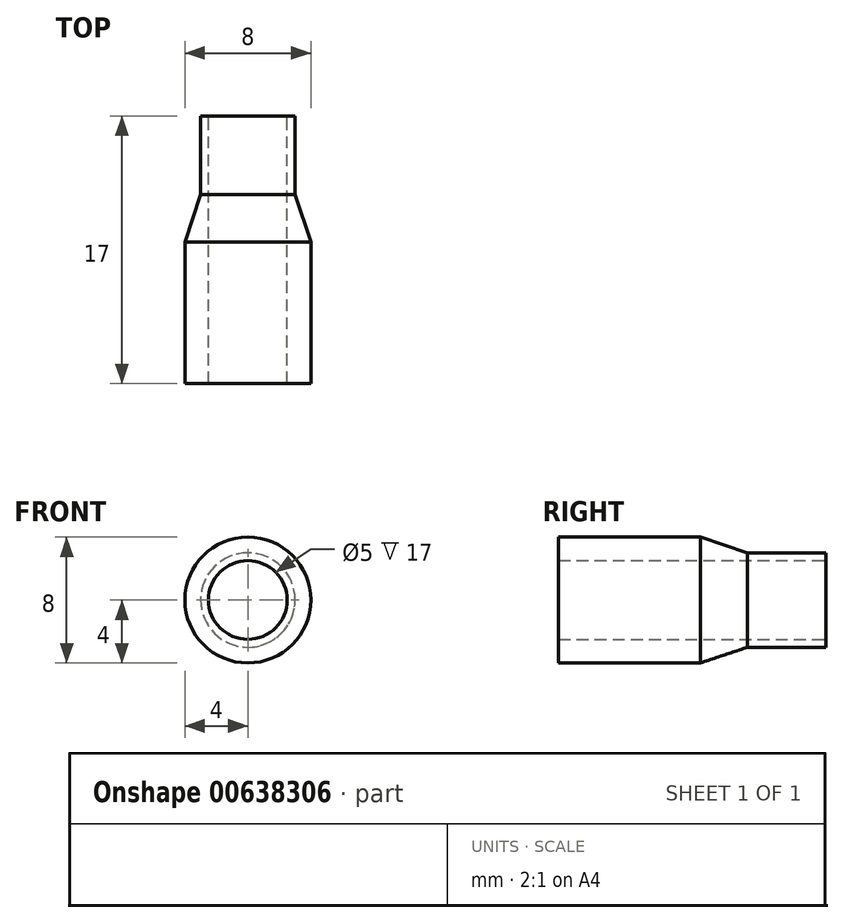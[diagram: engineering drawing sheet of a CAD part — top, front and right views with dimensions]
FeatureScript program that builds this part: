
annotation { "Feature Type Name" : "Feature", "Feature Type Description" : "" }
export const myFeature = defineFeature(function(context is Context, id is Id, definition is map)
    precondition{}
    {
        {
            var Q0;
            Q0=qCreatedBy(makeId("Front.planeOp"),FACE);
            var sketch = newSketch(context, id + "F0", { "sketchPlane" : qUnion([Q0])});
            skCircle(sketch, "E0", {"center": v(0, 0) * mm, "radius": 4 * mm});
            skCircle(sketch, "E1", {"center": v(0, 0) * mm, "radius": 2.5 * mm});
            skSolve(sketch);
        }
        {
            var Q0;
            Q0=makeQuery(id+"F0.imprint","IMPRINT",FACE,{"disambiguationData":[TD([[makeQuery(id+"F0.imprint","IMPRINT",EDGE,{"derivedFrom":sQuery(id+"F0.wireOp",EDGE,"E0")}),1.0]])]});
            extrude(context, id + "F1", {"entities" : qUnion([Q0]), "depth" : 12 * mm, "offsetDistance" : 25 * mm});
        }
        {
            var Q0;
            Q0=makeQuery(id+"F1.opExtrude","CAP_FACE",FACE,{"disambiguationData":[OSD([sQuery(id+"F0.wireOp",EDGE,"E0"),sQuery(id+"F0.wireOp",EDGE,"E1")])],"isStart":true});
            var sketch = newSketch(context, id + "F2", { "sketchPlane" : qUnion([Q0])});
            skCircle(sketch, "E2", {"center": v(0, 0) * mm, "radius": 2.5 * mm});
            skCircle(sketch, "E3", {"center": v(0, 0) * mm, "radius": 3 * mm});
            skSolve(sketch);
        }
        {
            var Q0;
            Q0 = qSketchRegion(id + "F2", true);
            extrude(context, id + "F3", {"entities" : qUnion([Q0]), "operationType" : NewBodyOperationType.ADD, "depth" : 5 * mm, "offsetDistance" : 25 * mm});
        }
        {
            var Q0;
            Q0=makeQuery(id+"F1.opExtrude","CAP_EDGE",EDGE,{"disambiguationData":[OSD([sQuery(id+"F0.wireOp",EDGE,"E0")])],"isStart":true});
            chamfer(context, id + "F4", {"entities" : qUnion([Q0]), "chamferType" : ChamferType.TWO_OFFSETS, "width1" : 3 * mm, "oppositeDirection" : false, "width2" : 1 * mm, "tangentPropagation" : true});
        }
    });
